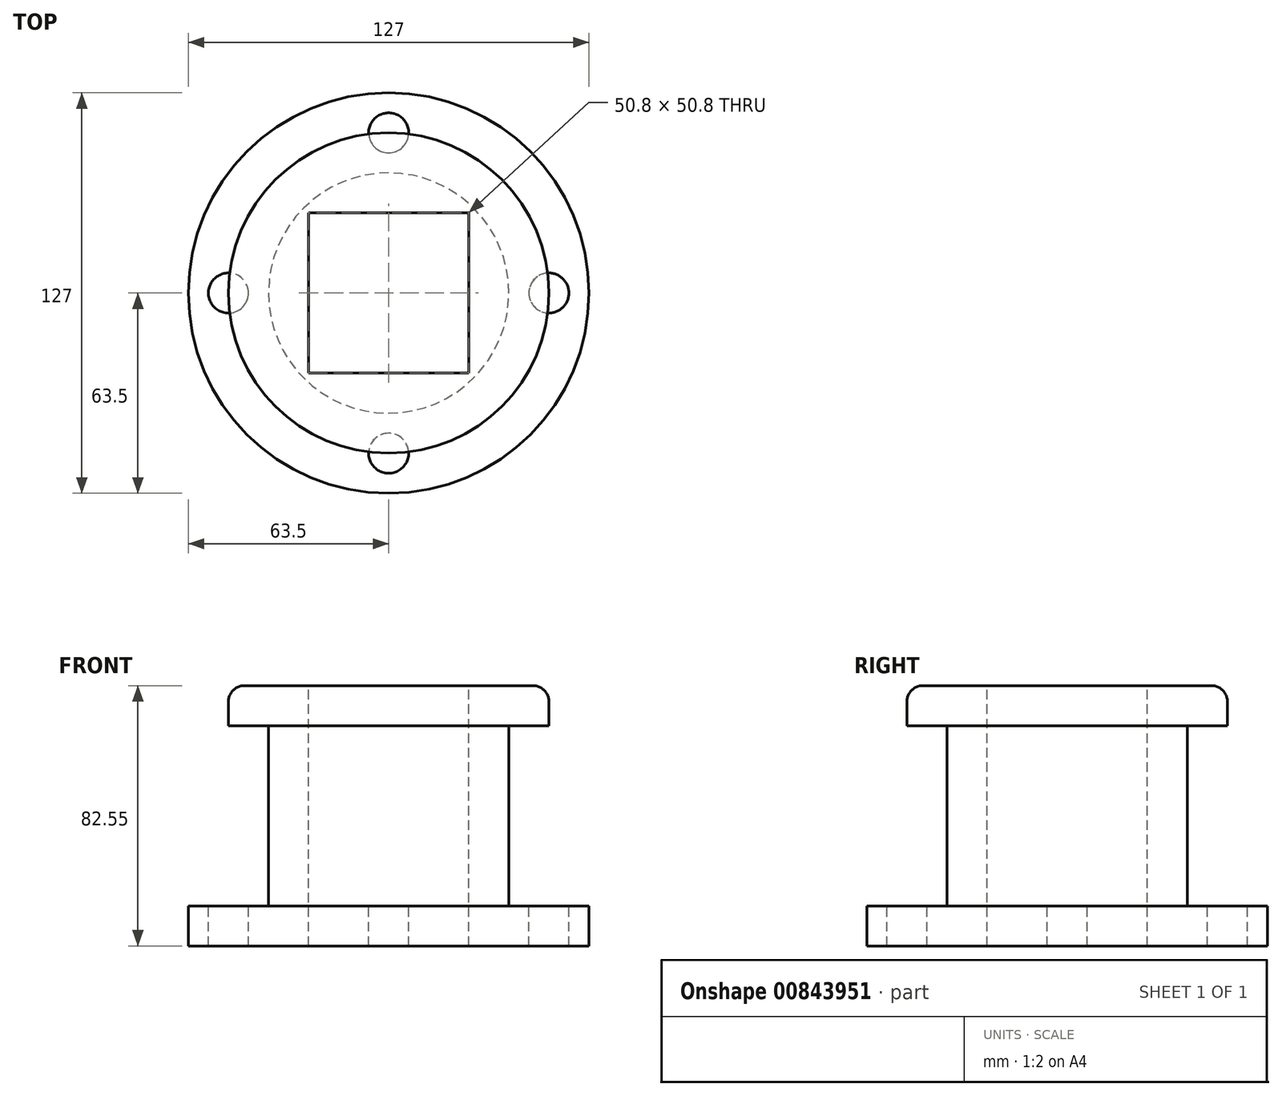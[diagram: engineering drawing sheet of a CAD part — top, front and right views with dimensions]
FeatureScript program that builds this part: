
annotation { "Feature Type Name" : "Feature", "Feature Type Description" : "" }
export const myFeature = defineFeature(function(context is Context, id is Id, definition is map)
    precondition{}
    {
        {
            var Q0;
            Q0=qCreatedBy(makeId("Top.planeOp"),FACE);
            var sketch = newSketch(context, id + "F0", { "sketchPlane" : qUnion([Q0])});
            skCircle(sketch, "E0", {"center": v(0, 0) * mm, "radius": 63.5 * mm});
            skSolve(sketch);
        }
        {
            var Q0;
            Q0 = qSketchRegion(id + "F0", true);
            extrude(context, id + "F1", {"entities" : qUnion([Q0]), "depth" : 12.7 * mm, "offsetDistance" : 25.4 * mm});
        }
        {
            var Q0;
            Q0=makeQuery(id+"F1.opExtrude","CAP_FACE",FACE,{"disambiguationData":[OSD([sQuery(id+"F0.wireOp",EDGE,"E0")])],"isStart":false});
            var sketch = newSketch(context, id + "F2", { "sketchPlane" : qUnion([Q0])});
            skCircle(sketch, "E1", {"center": v(0, 0) * mm, "radius": 38.1 * mm});
            skSolve(sketch);
        }
        {
            var Q0;
            Q0 = qSketchRegion(id + "F2", true);
            extrude(context, id + "F3", {"entities" : qUnion([Q0]), "operationType" : NewBodyOperationType.ADD, "depth" : 57.15 * mm, "offsetDistance" : 25.4 * mm});
        }
        {
            var Q0;
            Q0=makeQuery(id+"F1.opExtrude","CAP_FACE",FACE,{"disambiguationData":[OSD([sQuery(id+"F0.wireOp",EDGE,"E0")])],"isStart":false});
            var sketch = newSketch(context, id + "F4", { "sketchPlane" : qUnion([Q0])});
            skCircle(sketch, "E2", {"center": v(-50.8, 0) * mm, "radius": 6.35 * mm});
            skCircle(sketch, "E3", {"center": v(0, 50.8) * mm, "radius": 6.35 * mm});
            skCircle(sketch, "E4", {"center": v(50.8, 0) * mm, "radius": 6.35 * mm});
            skCircle(sketch, "E5", {"center": v(0, -50.8) * mm, "radius": 6.35 * mm});
            skPoint(sketch, "E6.start.orphan", {"position": v(63.5, 0) * mm});
            skPoint(sketch, "E7.start.orphan", {"position": v(0, 63.5) * mm});
            skPoint(sketch, "E8.orphan", {"position": v(-63.5, 0) * mm});
            skPoint(sketch, "E9.start.orphan", {"position": v(0, -63.5) * mm});
            skSolve(sketch);
        }
        {
            var Q0;
            Q0 = qSketchRegion(id + "F4", true);
            extrude(context, id + "F5", {"entities" : qUnion([Q0]), "operationType" : NewBodyOperationType.REMOVE, "oppositeDirection" : true, "depth" : 25.4 * mm, "offsetDistance" : 25.4 * mm});
        }
        {
            var Q0;
            Q0=makeQuery(id+"F3.opExtrude","CAP_FACE",FACE,{"disambiguationData":[OSD([sQuery(id+"F2.wireOp",EDGE,"E1")])],"isStart":false});
            var sketch = newSketch(context, id + "F6", { "sketchPlane" : qUnion([Q0])});
            skCircle(sketch, "E10", {"center": v(0, 0) * mm, "radius": 50.8 * mm});
            skSolve(sketch);
        }
        {
            var Q0;
            Q0 = qSketchRegion(id + "F6", true);
            extrude(context, id + "F7", {"entities" : qUnion([Q0]), "operationType" : NewBodyOperationType.ADD, "depth" : 12.7 * mm, "offsetDistance" : 25.4 * mm});
        }
        {
            var Q0;
            Q0=makeQuery(id+"F7.opExtrude","CAP_EDGE",EDGE,{"disambiguationData":[OSD([sQuery(id+"F6.wireOp",EDGE,"E10")])],"isStart":false});
            fillet(context, id + "F8", {"entities" : qUnion([Q0]), "radius" : 5.08 * mm, "tangentPropagation" : true, "allowEdgeOverflow" : false});
        }
        {
            var Q0;
            Q0=makeQuery(id+"F7.opExtrude","CAP_FACE",FACE,{"disambiguationData":[OSD([sQuery(id+"F6.wireOp",EDGE,"E10")])],"isStart":false});
            var sketch = newSketch(context, id + "F9", { "sketchPlane" : qUnion([Q0])});
            skLineSegment(sketch, "E11", {"start": v(-25.4, 0) * mm, "end": v(-25.4, -25.4) * mm});
            skLineSegment(sketch, "E12", {"start": v(-25.4, -25.4) * mm, "end": v(25.4, -25.4) * mm});
            skLineSegment(sketch, "E13", {"start": v(25.4, -25.4) * mm, "end": v(25.4, 25.4) * mm});
            skLineSegment(sketch, "E14", {"start": v(25.4, 25.4) * mm, "end": v(-25.4, 25.4) * mm});
            skLineSegment(sketch, "E15", {"start": v(-25.4, 25.4) * mm, "end": v(-25.4, 0) * mm});
            skPoint(sketch, "E16.start.orphan", {"position": v(0, 0) * mm});
            skSolve(sketch);
        }
        {
            var Q0;
            Q0 = qSketchRegion(id + "F9", true);
            extrude(context, id + "F10", {"entities" : qUnion([Q0]), "operationType" : NewBodyOperationType.REMOVE, "oppositeDirection" : true, "depth" : 127 * mm, "offsetDistance" : 25.4 * mm});
        }
    });
